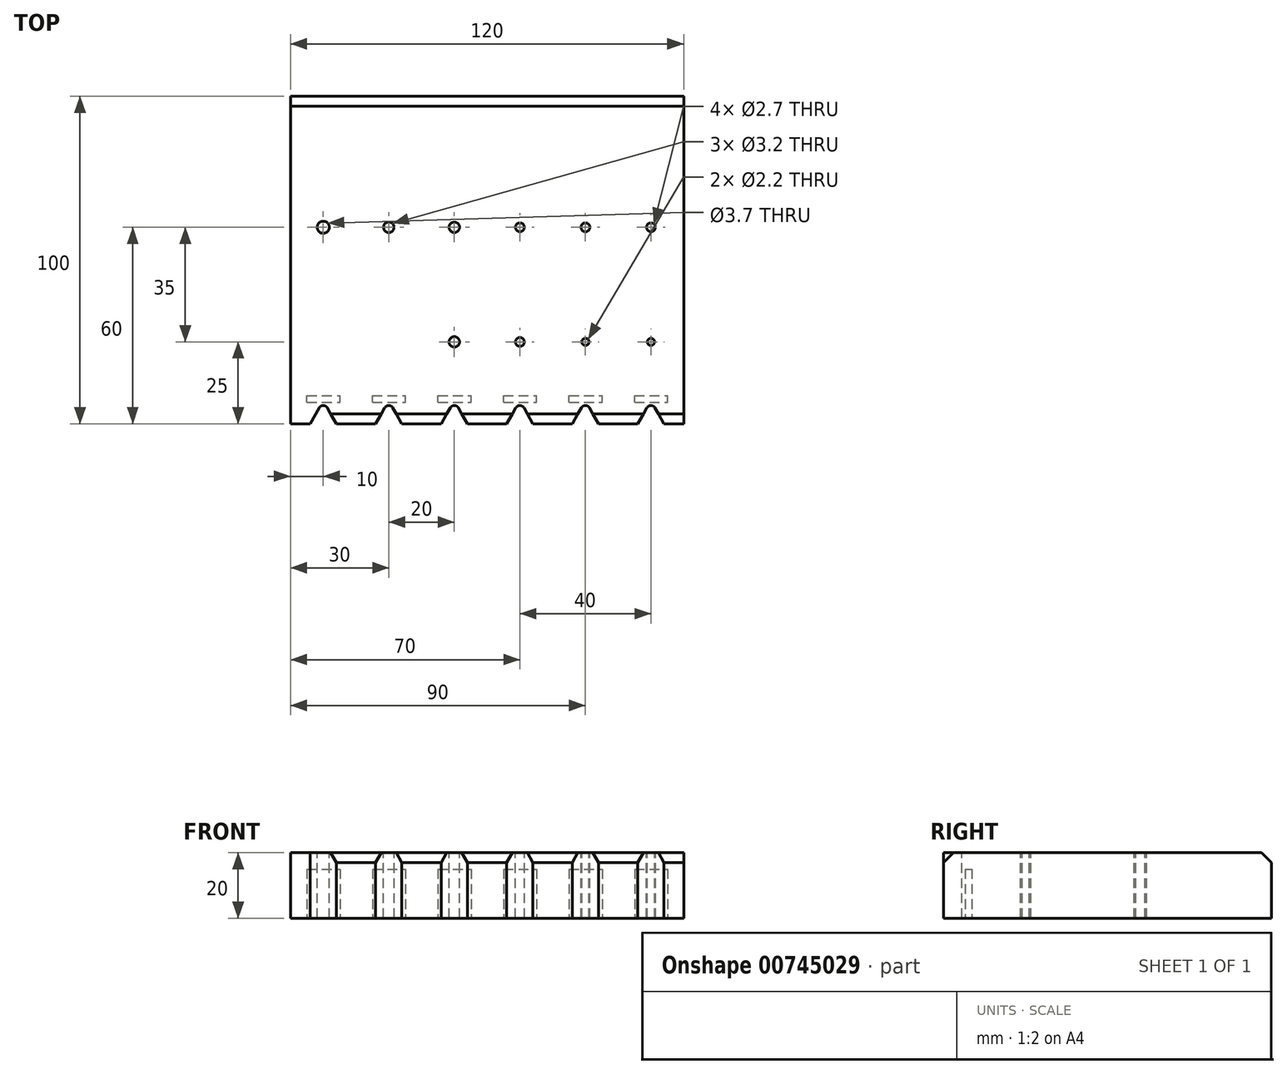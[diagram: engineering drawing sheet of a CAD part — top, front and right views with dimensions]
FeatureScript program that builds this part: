
annotation { "Feature Type Name" : "Feature", "Feature Type Description" : "" }
export const myFeature = defineFeature(function(context is Context, id is Id, definition is map)
    precondition{}
    {
        {
            var Q0;
            Q0=qCreatedBy(makeId("Top.planeOp"),FACE);
            var sketch = newSketch(context, id + "F0", { "sketchPlane" : qUnion([Q0])});
            skLineSegment(sketch, "E0.bottom", {"start": v(-40, -50) * mm, "end": v(-46, -50) * mm});
            skLineSegment(sketch, "E0.top", {"start": v(60, 50) * mm, "end": v(-60, 50) * mm});
            skLineSegment(sketch, "E0.left", {"start": v(60, -50) * mm, "end": v(60, 50) * mm});
            skLineSegment(sketch, "E0.right", {"start": v(-60, -50) * mm, "end": v(-60, 50) * mm});
            skPoint(sketch, "E0.middle", {"position": v(0, 0) * mm});
            skLineSegment(sketch, "E1", {"start": v(-60, -50) * mm, "end": v(-54, -50) * mm});
            skLineSegment(sketch, "E2", {"start": v(-46, -50) * mm, "end": v(-40, -50) * mm});
            skLineSegment(sketch, "E3.trimOffspring", {"start": v(-54, -50) * mm, "end": v(-60, -50) * mm});
            skLineSegment(sketch, "E4", {"start": v(-54, -50) * mm, "end": v(-50, -43) * mm});
            skLineSegment(sketch, "E5", {"start": v(-50, -43) * mm, "end": v(-46, -50) * mm});
            skLineSegment(sketch, "E6.1.0.0", {"start": v(-34, -50) * mm, "end": v(-40, -50) * mm});
            skLineSegment(sketch, "E6.1.0.1", {"start": v(-34, -50) * mm, "end": v(-30, -43) * mm});
            skLineSegment(sketch, "E6.1.0.2", {"start": v(-30, -43) * mm, "end": v(-26, -50) * mm});
            skLineSegment(sketch, "E6.1.0.3", {"start": v(-26, -50) * mm, "end": v(-20, -50) * mm});
            skLineSegment(sketch, "E6.2.0.0", {"start": v(-14, -50) * mm, "end": v(-20, -50) * mm});
            skLineSegment(sketch, "E6.2.0.1", {"start": v(-14, -50) * mm, "end": v(-10, -43) * mm});
            skLineSegment(sketch, "E6.2.0.2", {"start": v(-10, -43) * mm, "end": v(-6, -50) * mm});
            skLineSegment(sketch, "E6.2.0.3", {"start": v(-6, -50) * mm, "end": v(0, -50) * mm});
            skLineSegment(sketch, "E6.3.0.0", {"start": v(6, -50) * mm, "end": v(0, -50) * mm});
            skLineSegment(sketch, "E6.3.0.1", {"start": v(6, -50) * mm, "end": v(10, -43) * mm});
            skLineSegment(sketch, "E6.3.0.2", {"start": v(10, -43) * mm, "end": v(14, -50) * mm});
            skLineSegment(sketch, "E6.3.0.3", {"start": v(14, -50) * mm, "end": v(20, -50) * mm});
            skLineSegment(sketch, "E6.4.0.0", {"start": v(26, -50) * mm, "end": v(20, -50) * mm});
            skLineSegment(sketch, "E6.4.0.1", {"start": v(26, -50) * mm, "end": v(30, -43) * mm});
            skLineSegment(sketch, "E6.4.0.2", {"start": v(30, -43) * mm, "end": v(34, -50) * mm});
            skLineSegment(sketch, "E6.4.0.3", {"start": v(34, -50) * mm, "end": v(40, -50) * mm});
            skLineSegment(sketch, "E6.5.0.0", {"start": v(46, -50) * mm, "end": v(40, -50) * mm});
            skLineSegment(sketch, "E6.5.0.1", {"start": v(46, -50) * mm, "end": v(50, -43) * mm});
            skLineSegment(sketch, "E6.5.0.2", {"start": v(50, -43) * mm, "end": v(54, -50) * mm});
            skLineSegment(sketch, "E6.5.0.3", {"start": v(54, -50) * mm, "end": v(60, -50) * mm});
            skLineSegment(sketch, "E6.direction1", {"start": v(-60, -50) * mm, "end": v(-40, -50) * mm, "construction": true});
            skSolve(sketch);
        }
        {
            var Q0;
            Q0=makeQuery(id+"F0.imprint","IMPRINT",FACE,{"disambiguationData":[TD([[makeQuery(id+"F0.imprint","IMPRINT",EDGE,{"derivedFrom":sQuery(id+"F0.wireOp",EDGE,"E0.top")}),1.0]])]});
            extrude(context, id + "F1", {"entities" : qUnion([Q0]), "depth" : 20 * mm, "offsetDistance" : 25 * mm});
        }
        {
            var Q0;
            Q0=makeQuery(id+"F1.opExtrude","SWEPT_EDGE",EDGE,{"disambiguationData":[OSD([sQuery(id+"F0.wireOp",EDGE,"E4"),sQuery(id+"F0.wireOp",EDGE,"E5")])]});
            var Q1;
            Q1=makeQuery(id+"F1.opExtrude","SWEPT_EDGE",EDGE,{"disambiguationData":[OSD([sQuery(id+"F0.wireOp",EDGE,"E6.1.0.1"),sQuery(id+"F0.wireOp",EDGE,"E6.1.0.2")])]});
            var Q2;
            Q2=makeQuery(id+"F1.opExtrude","SWEPT_EDGE",EDGE,{"disambiguationData":[OSD([sQuery(id+"F0.wireOp",EDGE,"E6.2.0.1"),sQuery(id+"F0.wireOp",EDGE,"E6.2.0.2")])]});
            var Q3;
            Q3=makeQuery(id+"F1.opExtrude","SWEPT_EDGE",EDGE,{"disambiguationData":[OSD([sQuery(id+"F0.wireOp",EDGE,"E6.3.0.1"),sQuery(id+"F0.wireOp",EDGE,"E6.3.0.2")])]});
            var Q4;
            Q4=makeQuery(id+"F1.opExtrude","SWEPT_EDGE",EDGE,{"disambiguationData":[OSD([sQuery(id+"F0.wireOp",EDGE,"E6.4.0.1"),sQuery(id+"F0.wireOp",EDGE,"E6.4.0.2")])]});
            var Q5;
            Q5=makeQuery(id+"F1.opExtrude","SWEPT_EDGE",EDGE,{"disambiguationData":[OSD([sQuery(id+"F0.wireOp",EDGE,"E6.5.0.1"),sQuery(id+"F0.wireOp",EDGE,"E6.5.0.2")])]});
            fillet(context, id + "F2", {"entities" : qUnion([Q0, Q1, Q2, Q3, Q4, Q5]), "radius" : 1.4 * mm, "tangentPropagation" : true, "allowEdgeOverflow" : false});
        }
        {
            var Q0;
            Q0=makeQuery(id+"F1.opExtrude","CAP_FACE",FACE,{"disambiguationData":[OSD([sQuery(id+"F0.wireOp",EDGE,"E0.top"),sQuery(id+"F0.wireOp",EDGE,"E0.left"),sQuery(id+"F0.wireOp",EDGE,"E0.right"),sQuery(id+"F0.wireOp",EDGE,"E2"),sQuery(id+"F0.wireOp",EDGE,"E3.trimOffspring"),sQuery(id+"F0.wireOp",EDGE,"E4"),sQuery(id+"F0.wireOp",EDGE,"E5"),sQuery(id+"F0.wireOp",EDGE,"E6.1.0.0"),sQuery(id+"F0.wireOp",EDGE,"E6.1.0.1"),sQuery(id+"F0.wireOp",EDGE,"E6.1.0.2"),sQuery(id+"F0.wireOp",EDGE,"E6.1.0.3"),sQuery(id+"F0.wireOp",EDGE,"E6.2.0.0"),sQuery(id+"F0.wireOp",EDGE,"E6.2.0.1"),sQuery(id+"F0.wireOp",EDGE,"E6.2.0.2"),sQuery(id+"F0.wireOp",EDGE,"E6.2.0.3"),sQuery(id+"F0.wireOp",EDGE,"E6.3.0.0"),sQuery(id+"F0.wireOp",EDGE,"E6.3.0.1"),sQuery(id+"F0.wireOp",EDGE,"E6.3.0.2"),sQuery(id+"F0.wireOp",EDGE,"E6.3.0.3"),sQuery(id+"F0.wireOp",EDGE,"E6.4.0.0"),sQuery(id+"F0.wireOp",EDGE,"E6.4.0.1"),sQuery(id+"F0.wireOp",EDGE,"E6.4.0.2"),sQuery(id+"F0.wireOp",EDGE,"E6.4.0.3"),sQuery(id+"F0.wireOp",EDGE,"E6.5.0.0"),sQuery(id+"F0.wireOp",EDGE,"E6.5.0.1"),sQuery(id+"F0.wireOp",EDGE,"E6.5.0.2"),sQuery(id+"F0.wireOp",EDGE,"E6.5.0.3")])],"isStart":true});
            var sketch = newSketch(context, id + "F3", { "sketchPlane" : qUnion([Q0])});
            skLineSegment(sketch, "E7.bottom", {"start": v(-55, 43.5) * mm, "end": v(-44.9, 43.5) * mm});
            skLineSegment(sketch, "E7.top", {"start": v(-55, 41.4) * mm, "end": v(-44.9, 41.4) * mm});
            skLineSegment(sketch, "E7.left", {"start": v(-55, 43.5) * mm, "end": v(-55, 41.4) * mm});
            skLineSegment(sketch, "E7.right", {"start": v(-44.9, 43.5) * mm, "end": v(-44.9, 41.4) * mm});
            skLineSegment(sketch, "E8.1.0.0", {"start": v(-35, 43.5) * mm, "end": v(-24.9, 43.5) * mm});
            skLineSegment(sketch, "E8.1.0.1", {"start": v(-35, 41.4) * mm, "end": v(-24.9, 41.4) * mm});
            skLineSegment(sketch, "E8.1.0.2", {"start": v(-35, 43.5) * mm, "end": v(-35, 41.4) * mm});
            skLineSegment(sketch, "E8.1.0.3", {"start": v(-24.9, 43.5) * mm, "end": v(-24.9, 41.4) * mm});
            skLineSegment(sketch, "E8.2.0.0", {"start": v(-15, 43.5) * mm, "end": v(-4.9, 43.5) * mm});
            skLineSegment(sketch, "E8.2.0.1", {"start": v(-15, 41.4) * mm, "end": v(-4.9, 41.4) * mm});
            skLineSegment(sketch, "E8.2.0.2", {"start": v(-15, 43.5) * mm, "end": v(-15, 41.4) * mm});
            skLineSegment(sketch, "E8.2.0.3", {"start": v(-4.9, 43.5) * mm, "end": v(-4.9, 41.4) * mm});
            skLineSegment(sketch, "E8.3.0.0", {"start": v(5, 43.5) * mm, "end": v(15.1, 43.5) * mm});
            skLineSegment(sketch, "E8.3.0.1", {"start": v(5, 41.4) * mm, "end": v(15.1, 41.4) * mm});
            skLineSegment(sketch, "E8.3.0.2", {"start": v(5, 43.5) * mm, "end": v(5, 41.4) * mm});
            skLineSegment(sketch, "E8.3.0.3", {"start": v(15.1, 43.5) * mm, "end": v(15.1, 41.4) * mm});
            skLineSegment(sketch, "E8.4.0.0", {"start": v(25, 43.5) * mm, "end": v(35.1, 43.5) * mm});
            skLineSegment(sketch, "E8.4.0.1", {"start": v(25, 41.4) * mm, "end": v(35.1, 41.4) * mm});
            skLineSegment(sketch, "E8.4.0.2", {"start": v(25, 43.5) * mm, "end": v(25, 41.4) * mm});
            skLineSegment(sketch, "E8.4.0.3", {"start": v(35.1, 43.5) * mm, "end": v(35.1, 41.4) * mm});
            skLineSegment(sketch, "E8.5.0.0", {"start": v(45, 43.5) * mm, "end": v(55.1, 43.5) * mm});
            skLineSegment(sketch, "E8.5.0.1", {"start": v(45, 41.4) * mm, "end": v(55.1, 41.4) * mm});
            skLineSegment(sketch, "E8.5.0.2", {"start": v(45, 43.5) * mm, "end": v(45, 41.4) * mm});
            skLineSegment(sketch, "E8.5.0.3", {"start": v(55.1, 43.5) * mm, "end": v(55.1, 41.4) * mm});
            skLineSegment(sketch, "E8.direction1", {"start": v(-55, 43.5) * mm, "end": v(-35, 43.5) * mm, "construction": true});
            skSolve(sketch);
        }
        {
            var Q0;
            Q0 = qSketchRegion(id + "F3", true);
            extrude(context, id + "F4", {"entities" : qUnion([Q0]), "operationType" : NewBodyOperationType.REMOVE, "oppositeDirection" : true, "depth" : 15 * mm, "offsetDistance" : 25 * mm});
        }
        {
            var Q0;
            Q0=makeQuery(id+"F1.opExtrude","CAP_EDGE",EDGE,{"disambiguationData":[OSD([sQuery(id+"F0.wireOp",EDGE,"E0.top")])],"isStart":false});
            var Q1;
            Q1=makeQuery(id+"F1.opExtrude","CAP_EDGE",EDGE,{"disambiguationData":[OSD([sQuery(id+"F0.wireOp",EDGE,"E2"),sQuery(id+"F0.wireOp",EDGE,"E6.1.0.0")])],"isStart":false});
            var Q2;
            Q2=makeQuery(id+"F1.opExtrude","CAP_EDGE",EDGE,{"disambiguationData":[OSD([sQuery(id+"F0.wireOp",EDGE,"E3.trimOffspring")])],"isStart":false});
            var Q3;
            Q3=makeQuery(id+"F1.opExtrude","CAP_EDGE",EDGE,{"disambiguationData":[OSD([sQuery(id+"F0.wireOp",EDGE,"E6.1.0.3"),sQuery(id+"F0.wireOp",EDGE,"E6.2.0.0")])],"isStart":false});
            var Q4;
            Q4=makeQuery(id+"F1.opExtrude","CAP_EDGE",EDGE,{"disambiguationData":[OSD([sQuery(id+"F0.wireOp",EDGE,"E6.2.0.3"),sQuery(id+"F0.wireOp",EDGE,"E6.3.0.0")])],"isStart":false});
            var Q5;
            Q5=makeQuery(id+"F1.opExtrude","CAP_EDGE",EDGE,{"disambiguationData":[OSD([sQuery(id+"F0.wireOp",EDGE,"E6.3.0.3"),sQuery(id+"F0.wireOp",EDGE,"E6.4.0.0")])],"isStart":false});
            var Q6;
            Q6=makeQuery(id+"F1.opExtrude","CAP_EDGE",EDGE,{"disambiguationData":[OSD([sQuery(id+"F0.wireOp",EDGE,"E6.4.0.3"),sQuery(id+"F0.wireOp",EDGE,"E6.5.0.0")])],"isStart":false});
            var Q7;
            Q7=makeQuery(id+"F1.opExtrude","CAP_EDGE",EDGE,{"disambiguationData":[OSD([sQuery(id+"F0.wireOp",EDGE,"E6.5.0.3")])],"isStart":false});
            chamfer(context, id + "F5", {"entities" : qUnion([Q0, Q1, Q2, Q3, Q4, Q5, Q6, Q7]), "width" : 3 * mm, "tangentPropagation" : true});
        }
        {
            var Q0;
            Q0=makeQuery(id+"F1.opExtrude","CAP_FACE",FACE,{"disambiguationData":[OSD([sQuery(id+"F0.wireOp",EDGE,"E0.top"),sQuery(id+"F0.wireOp",EDGE,"E0.left"),sQuery(id+"F0.wireOp",EDGE,"E0.right"),sQuery(id+"F0.wireOp",EDGE,"E2"),sQuery(id+"F0.wireOp",EDGE,"E3.trimOffspring"),sQuery(id+"F0.wireOp",EDGE,"E4"),sQuery(id+"F0.wireOp",EDGE,"E5"),sQuery(id+"F0.wireOp",EDGE,"E6.1.0.0"),sQuery(id+"F0.wireOp",EDGE,"E6.1.0.1"),sQuery(id+"F0.wireOp",EDGE,"E6.1.0.2"),sQuery(id+"F0.wireOp",EDGE,"E6.1.0.3"),sQuery(id+"F0.wireOp",EDGE,"E6.2.0.0"),sQuery(id+"F0.wireOp",EDGE,"E6.2.0.1"),sQuery(id+"F0.wireOp",EDGE,"E6.2.0.2"),sQuery(id+"F0.wireOp",EDGE,"E6.2.0.3"),sQuery(id+"F0.wireOp",EDGE,"E6.3.0.0"),sQuery(id+"F0.wireOp",EDGE,"E6.3.0.1"),sQuery(id+"F0.wireOp",EDGE,"E6.3.0.2"),sQuery(id+"F0.wireOp",EDGE,"E6.3.0.3"),sQuery(id+"F0.wireOp",EDGE,"E6.4.0.0"),sQuery(id+"F0.wireOp",EDGE,"E6.4.0.1"),sQuery(id+"F0.wireOp",EDGE,"E6.4.0.2"),sQuery(id+"F0.wireOp",EDGE,"E6.4.0.3"),sQuery(id+"F0.wireOp",EDGE,"E6.5.0.0"),sQuery(id+"F0.wireOp",EDGE,"E6.5.0.1"),sQuery(id+"F0.wireOp",EDGE,"E6.5.0.2"),sQuery(id+"F0.wireOp",EDGE,"E6.5.0.3")])],"isStart":false});
            var sketch = newSketch(context, id + "F6", { "sketchPlane" : qUnion([Q0])});
            skLineSegment(sketch, "E9", {"start": v(-75, 10) * mm, "end": v(75, 10) * mm, "construction": true});
            skPoint(sketch, "E10", {"position": v(-50, 10) * mm});
            skPoint(sketch, "E11.1.0.0", {"position": v(-30, 10) * mm});
            skPoint(sketch, "E11.2.0.0", {"position": v(-10, 10) * mm});
            skPoint(sketch, "E11.3.0.0", {"position": v(10, 10) * mm});
            skPoint(sketch, "E11.4.0.0", {"position": v(30, 10) * mm});
            skPoint(sketch, "E11.5.0.0", {"position": v(50, 10) * mm});
            skLineSegment(sketch, "E11.direction1", {"start": v(-50, 10) * mm, "end": v(-30, 10) * mm, "construction": true});
            skLineSegment(sketch, "E12", {"start": v(-75, -25) * mm, "end": v(75, -25) * mm, "construction": true});
            skPoint(sketch, "E13", {"position": v(-50, -25) * mm});
            skPoint(sketch, "E14.1.0.0", {"position": v(-30, -25) * mm});
            skPoint(sketch, "E14.2.0.0", {"position": v(-10, -25) * mm});
            skPoint(sketch, "E14.3.0.0", {"position": v(10, -25) * mm});
            skPoint(sketch, "E14.4.0.0", {"position": v(30, -25) * mm});
            skPoint(sketch, "E14.5.0.0", {"position": v(50, -25) * mm});
            skLineSegment(sketch, "E14.direction1", {"start": v(-50, -25) * mm, "end": v(-30, -25) * mm, "construction": true});
            skSolve(sketch);
        }
        {
            var Q0;
            Q0=sQuery(id+"F6.wireOp",VERTEX,"E14.5.0.0");
            var Q1;
            Q1=sQuery(id+"F6.wireOp",VERTEX,"E14.4.0.0");
            var Q2;
            Q2=makeQuery(id+"F1.opExtrude","SWEPT_BODY",BODY,{"disambiguationData":[OSD([sQuery(id+"F0.wireOp",EDGE,"E0.top"),sQuery(id+"F0.wireOp",EDGE,"E0.left"),sQuery(id+"F0.wireOp",EDGE,"E0.right"),sQuery(id+"F0.wireOp",EDGE,"E2"),sQuery(id+"F0.wireOp",EDGE,"E3.trimOffspring"),sQuery(id+"F0.wireOp",EDGE,"E4"),sQuery(id+"F0.wireOp",EDGE,"E5"),sQuery(id+"F0.wireOp",EDGE,"E6.1.0.0"),sQuery(id+"F0.wireOp",EDGE,"E6.1.0.1"),sQuery(id+"F0.wireOp",EDGE,"E6.1.0.2"),sQuery(id+"F0.wireOp",EDGE,"E6.1.0.3"),sQuery(id+"F0.wireOp",EDGE,"E6.2.0.0"),sQuery(id+"F0.wireOp",EDGE,"E6.2.0.1"),sQuery(id+"F0.wireOp",EDGE,"E6.2.0.2"),sQuery(id+"F0.wireOp",EDGE,"E6.2.0.3"),sQuery(id+"F0.wireOp",EDGE,"E6.3.0.0"),sQuery(id+"F0.wireOp",EDGE,"E6.3.0.1"),sQuery(id+"F0.wireOp",EDGE,"E6.3.0.2"),sQuery(id+"F0.wireOp",EDGE,"E6.3.0.3"),sQuery(id+"F0.wireOp",EDGE,"E6.4.0.0"),sQuery(id+"F0.wireOp",EDGE,"E6.4.0.1"),sQuery(id+"F0.wireOp",EDGE,"E6.4.0.2"),sQuery(id+"F0.wireOp",EDGE,"E6.4.0.3"),sQuery(id+"F0.wireOp",EDGE,"E6.5.0.0"),sQuery(id+"F0.wireOp",EDGE,"E6.5.0.1"),sQuery(id+"F0.wireOp",EDGE,"E6.5.0.2"),sQuery(id+"F0.wireOp",EDGE,"E6.5.0.3")])]});
            hole(context, id + "F7", {"style" : HoleStyle.SIMPLE, "endStyle" : HoleEndStyle.THROUGH, "holeDiameter" : 2.2 * mm, "majorDiameter" : 5 * mm, "isTappedThrough" : true, "tappedDepth" : 6 * mm, "tapClearance" : 3, "locations" : qUnion([Q0, Q1]), "scope" : qUnion([Q2])});
        }
        {
            var Q0;
            Q0=sQuery(id+"F6.wireOp",VERTEX,"E11.5.0.0");
            var Q1;
            Q1=sQuery(id+"F6.wireOp",VERTEX,"E11.4.0.0");
            var Q2;
            Q2=sQuery(id+"F6.wireOp",VERTEX,"E11.3.0.0");
            var Q3;
            Q3=sQuery(id+"F6.wireOp",VERTEX,"E14.3.0.0");
            var Q4;
            Q4=makeQuery(id+"F1.opExtrude","SWEPT_BODY",BODY,{"disambiguationData":[OSD([sQuery(id+"F0.wireOp",EDGE,"E0.top"),sQuery(id+"F0.wireOp",EDGE,"E0.left"),sQuery(id+"F0.wireOp",EDGE,"E0.right"),sQuery(id+"F0.wireOp",EDGE,"E2"),sQuery(id+"F0.wireOp",EDGE,"E3.trimOffspring"),sQuery(id+"F0.wireOp",EDGE,"E4"),sQuery(id+"F0.wireOp",EDGE,"E5"),sQuery(id+"F0.wireOp",EDGE,"E6.1.0.0"),sQuery(id+"F0.wireOp",EDGE,"E6.1.0.1"),sQuery(id+"F0.wireOp",EDGE,"E6.1.0.2"),sQuery(id+"F0.wireOp",EDGE,"E6.1.0.3"),sQuery(id+"F0.wireOp",EDGE,"E6.2.0.0"),sQuery(id+"F0.wireOp",EDGE,"E6.2.0.1"),sQuery(id+"F0.wireOp",EDGE,"E6.2.0.2"),sQuery(id+"F0.wireOp",EDGE,"E6.2.0.3"),sQuery(id+"F0.wireOp",EDGE,"E6.3.0.0"),sQuery(id+"F0.wireOp",EDGE,"E6.3.0.1"),sQuery(id+"F0.wireOp",EDGE,"E6.3.0.2"),sQuery(id+"F0.wireOp",EDGE,"E6.3.0.3"),sQuery(id+"F0.wireOp",EDGE,"E6.4.0.0"),sQuery(id+"F0.wireOp",EDGE,"E6.4.0.1"),sQuery(id+"F0.wireOp",EDGE,"E6.4.0.2"),sQuery(id+"F0.wireOp",EDGE,"E6.4.0.3"),sQuery(id+"F0.wireOp",EDGE,"E6.5.0.0"),sQuery(id+"F0.wireOp",EDGE,"E6.5.0.1"),sQuery(id+"F0.wireOp",EDGE,"E6.5.0.2"),sQuery(id+"F0.wireOp",EDGE,"E6.5.0.3")])]});
            hole(context, id + "F8", {"style" : HoleStyle.SIMPLE, "endStyle" : HoleEndStyle.THROUGH, "holeDiameter" : 2.7 * mm, "majorDiameter" : 5 * mm, "isTappedThrough" : true, "tappedDepth" : 6 * mm, "tapClearance" : 3, "locations" : qUnion([Q0, Q1, Q2, Q3]), "scope" : qUnion([Q4])});
        }
        {
            var Q0;
            Q0=sQuery(id+"F6.wireOp",VERTEX,"E11.2.0.0");
            var Q1;
            Q1=sQuery(id+"F6.wireOp",VERTEX,"E11.1.0.0");
            var Q2;
            Q2=sQuery(id+"F6.wireOp",VERTEX,"E14.2.0.0");
            var Q3;
            Q3=makeQuery(id+"F1.opExtrude","SWEPT_BODY",BODY,{"disambiguationData":[OSD([sQuery(id+"F0.wireOp",EDGE,"E0.top"),sQuery(id+"F0.wireOp",EDGE,"E0.left"),sQuery(id+"F0.wireOp",EDGE,"E0.right"),sQuery(id+"F0.wireOp",EDGE,"E2"),sQuery(id+"F0.wireOp",EDGE,"E3.trimOffspring"),sQuery(id+"F0.wireOp",EDGE,"E4"),sQuery(id+"F0.wireOp",EDGE,"E5"),sQuery(id+"F0.wireOp",EDGE,"E6.1.0.0"),sQuery(id+"F0.wireOp",EDGE,"E6.1.0.1"),sQuery(id+"F0.wireOp",EDGE,"E6.1.0.2"),sQuery(id+"F0.wireOp",EDGE,"E6.1.0.3"),sQuery(id+"F0.wireOp",EDGE,"E6.2.0.0"),sQuery(id+"F0.wireOp",EDGE,"E6.2.0.1"),sQuery(id+"F0.wireOp",EDGE,"E6.2.0.2"),sQuery(id+"F0.wireOp",EDGE,"E6.2.0.3"),sQuery(id+"F0.wireOp",EDGE,"E6.3.0.0"),sQuery(id+"F0.wireOp",EDGE,"E6.3.0.1"),sQuery(id+"F0.wireOp",EDGE,"E6.3.0.2"),sQuery(id+"F0.wireOp",EDGE,"E6.3.0.3"),sQuery(id+"F0.wireOp",EDGE,"E6.4.0.0"),sQuery(id+"F0.wireOp",EDGE,"E6.4.0.1"),sQuery(id+"F0.wireOp",EDGE,"E6.4.0.2"),sQuery(id+"F0.wireOp",EDGE,"E6.4.0.3"),sQuery(id+"F0.wireOp",EDGE,"E6.5.0.0"),sQuery(id+"F0.wireOp",EDGE,"E6.5.0.1"),sQuery(id+"F0.wireOp",EDGE,"E6.5.0.2"),sQuery(id+"F0.wireOp",EDGE,"E6.5.0.3")])]});
            hole(context, id + "F9", {"style" : HoleStyle.SIMPLE, "endStyle" : HoleEndStyle.THROUGH, "holeDiameter" : 3.2 * mm, "majorDiameter" : 5 * mm, "isTappedThrough" : true, "tappedDepth" : 6 * mm, "tapClearance" : 3, "locations" : qUnion([Q0, Q1, Q2]), "scope" : qUnion([Q3])});
        }
        {
            var Q0;
            Q0=sQuery(id+"F6.wireOp",VERTEX,"E10");
            var Q1;
            Q1=makeQuery(id+"F1.opExtrude","SWEPT_BODY",BODY,{"disambiguationData":[OSD([sQuery(id+"F0.wireOp",EDGE,"E0.top"),sQuery(id+"F0.wireOp",EDGE,"E0.left"),sQuery(id+"F0.wireOp",EDGE,"E0.right"),sQuery(id+"F0.wireOp",EDGE,"E2"),sQuery(id+"F0.wireOp",EDGE,"E3.trimOffspring"),sQuery(id+"F0.wireOp",EDGE,"E4"),sQuery(id+"F0.wireOp",EDGE,"E5"),sQuery(id+"F0.wireOp",EDGE,"E6.1.0.0"),sQuery(id+"F0.wireOp",EDGE,"E6.1.0.1"),sQuery(id+"F0.wireOp",EDGE,"E6.1.0.2"),sQuery(id+"F0.wireOp",EDGE,"E6.1.0.3"),sQuery(id+"F0.wireOp",EDGE,"E6.2.0.0"),sQuery(id+"F0.wireOp",EDGE,"E6.2.0.1"),sQuery(id+"F0.wireOp",EDGE,"E6.2.0.2"),sQuery(id+"F0.wireOp",EDGE,"E6.2.0.3"),sQuery(id+"F0.wireOp",EDGE,"E6.3.0.0"),sQuery(id+"F0.wireOp",EDGE,"E6.3.0.1"),sQuery(id+"F0.wireOp",EDGE,"E6.3.0.2"),sQuery(id+"F0.wireOp",EDGE,"E6.3.0.3"),sQuery(id+"F0.wireOp",EDGE,"E6.4.0.0"),sQuery(id+"F0.wireOp",EDGE,"E6.4.0.1"),sQuery(id+"F0.wireOp",EDGE,"E6.4.0.2"),sQuery(id+"F0.wireOp",EDGE,"E6.4.0.3"),sQuery(id+"F0.wireOp",EDGE,"E6.5.0.0"),sQuery(id+"F0.wireOp",EDGE,"E6.5.0.1"),sQuery(id+"F0.wireOp",EDGE,"E6.5.0.2"),sQuery(id+"F0.wireOp",EDGE,"E6.5.0.3")])]});
            hole(context, id + "F10", {"style" : HoleStyle.SIMPLE, "endStyle" : HoleEndStyle.THROUGH, "holeDiameter" : 3.7 * mm, "majorDiameter" : 5 * mm, "isTappedThrough" : true, "tappedDepth" : 6 * mm, "tapClearance" : 3, "locations" : qUnion([Q0]), "scope" : qUnion([Q1])});
        }
    });
